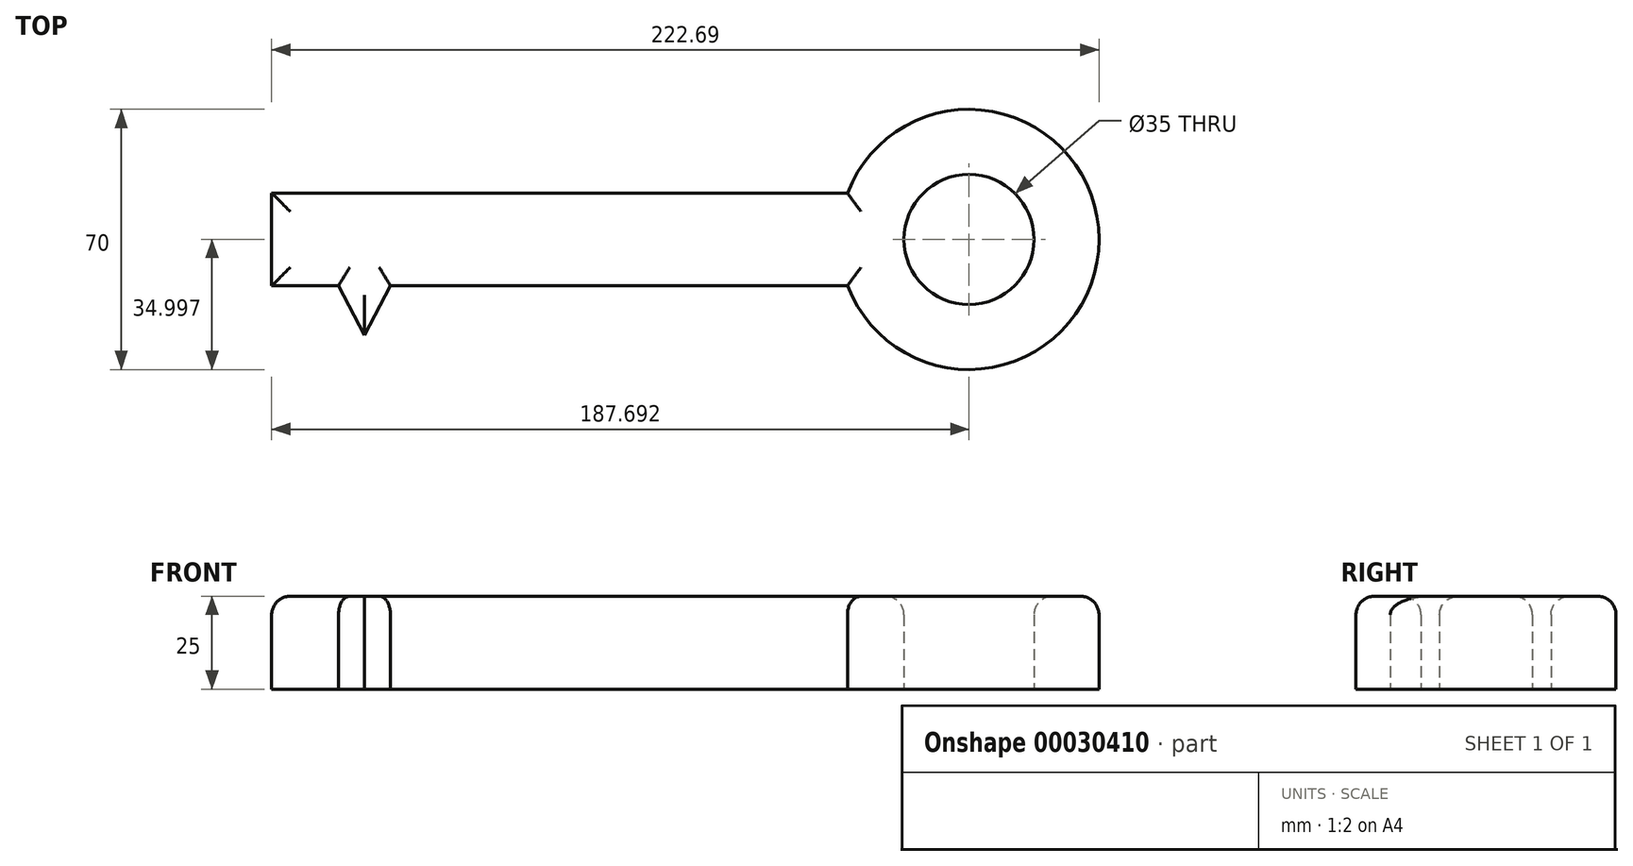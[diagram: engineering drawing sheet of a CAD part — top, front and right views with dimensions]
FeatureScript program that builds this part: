
annotation { "Feature Type Name" : "Feature", "Feature Type Description" : "" }
export const myFeature = defineFeature(function(context is Context, id is Id, definition is map)
    precondition{}
    {
        {
            var Q0;
            Q0=qCreatedBy(makeId("Top.planeOp"),FACE);
            var sketch = newSketch(context, id + "F0", { "sketchPlane" : qUnion([Q0])});
            skLineSegment(sketch, "E0.bottom", {"start": v(-155, 3.98) * mm, "end": v(0, 3.98) * mm});
            skLineSegment(sketch, "E0.top", {"start": v(-155, -21.02) * mm, "end": v(0, -21.02) * mm});
            skLineSegment(sketch, "E0.left", {"start": v(-155, 3.98) * mm, "end": v(-155, -21.02) * mm});
            skLineSegment(sketch, "E1.bottom", {"start": v(-155, -21.02) * mm, "end": v(-145, -21.02) * mm});
            skLineSegment(sketch, "E1.top", {"start": v(-155, -51.02) * mm, "end": v(-145, -51.02) * mm});
            skLineSegment(sketch, "E1.left", {"start": v(-155, -21.02) * mm, "end": v(-155, -51.02) * mm});
            skLineSegment(sketch, "E1.right", {"start": v(-145, -21.02) * mm, "end": v(-145, -51.02) * mm});
            skLineSegment(sketch, "E2.bottom", {"start": v(-155, -21.02) * mm, "end": v(-147, -21.02) * mm});
            skLineSegment(sketch, "E2.top", {"start": v(-155, -36.02) * mm, "end": v(-147, -36.02) * mm});
            skLineSegment(sketch, "E2.left", {"start": v(-155, -21.02) * mm, "end": v(-155, -36.02) * mm});
            skLineSegment(sketch, "E2.right", {"start": v(-147, -21.02) * mm, "end": v(-147, -36.02) * mm});
            skLineSegment(sketch, "E3", {"start": v(-137, -21.02) * mm, "end": v(-130, -34.29) * mm});
            skLineSegment(sketch, "E4", {"start": v(-130, -34.29) * mm, "end": v(-123, -21.02) * mm});
            skArc(sketch, "E5", {"start": v(0, -21.02) * mm, "mid": v(67.7, -8.52) * mm, "end": v(0, 3.98) * mm});
            skCircle(sketch, "E6", {"center": v(32.7, -8.52) * mm, "radius": 17.5 * mm});
            skLineSegment(sketch, "E7", {"start": v(-155, -8.52) * mm, "end": v(32.7, -8.52) * mm, "construction": true});
            skSolve(sketch);
        }
        {
            var Q0;
            Q0=makeQuery(id+"F0.imprint","IMPRINT",FACE,{"disambiguationData":[TD([[makeQuery(id+"F0.imprint","IMPRINT",EDGE,{"derivedFrom":sQuery(id+"F0.wireOp",EDGE,"E0.bottom")}),-1.0]])]});
            var Q1;
            Q1=makeQuery(id+"F0.imprint","IMPRINT",FACE,{"disambiguationData":[TD([[makeQuery(id+"F0.imprint","IMPRINT",EDGE,{"derivedFrom":sQuery(id+"F0.wireOp",EDGE,"E2.bottom")}),-1.0]])]});
            var Q2;
            Q2=makeQuery(id+"F0.imprint","IMPRINT",FACE,{"disambiguationData":[TD([[makeQuery(id+"F0.imprint","IMPRINT",EDGE,{"derivedFrom":sQuery(id+"F0.wireOp",EDGE,"E1.bottom")}),-1.0]])]});
            var Q3;
            {var subQ1=sQuery(id+"F0.wireOp",EDGE,"E3");Q3=makeQuery(id+"F0.imprint","IMPRINT",FACE,{"disambiguationData":[TD([[makeQuery(id+"F0.imprint","IMPRINT",EDGE,{"derivedFrom":subQ1}),1.0]])]});}
            extrude(context, id + "F1", {"entities" : qUnion([Q0, Q1, Q2, Q3]), "depth" : 25 * mm});
        }
        {
            var Q0;
            Q0=makeQuery(id+"F1.opExtrude","CAP_EDGE",EDGE,{"disambiguationData":[OSD([sQuery(id+"F0.wireOp",EDGE,"E0.bottom")])],"isStart":false});
            var Q1;
            {var subQ0=sQuery(id+"F0.wireOp",EDGE,"E0.top");Q1=makeQuery(id+"F1.opExtrude","CAP_EDGE",EDGE,{"disambiguationData":[OSD([subQ0]),TDD([makeQuery(id+"F0.imprint","IMPRINT",EDGE,{"disambiguationData":[TD([[makeQuery(id+"F0.imprint","INTERSECT",VERTEX,{"derivedFrom":[subQ0,sQuery(id+"F0.wireOp",EDGE,"E5")]}),1.0]])],"derivedFrom":subQ0})])],"isStart":false});}
            var Q2;
            Q2=makeQuery(id+"F1.opExtrude","CAP_EDGE",EDGE,{"disambiguationData":[OSD([sQuery(id+"F0.wireOp",EDGE,"E3")])],"isStart":false});
            var Q3;
            Q3=makeQuery(id+"F1.opExtrude","CAP_EDGE",EDGE,{"disambiguationData":[OSD([sQuery(id+"F0.wireOp",EDGE,"E0.left"),sQuery(id+"F0.wireOp",EDGE,"E1.left"),sQuery(id+"F0.wireOp",EDGE,"E2.left")])],"isStart":false});
            var Q4;
            Q4=makeQuery(id+"F1.opExtrude","CAP_EDGE",EDGE,{"disambiguationData":[OSD([sQuery(id+"F0.wireOp",EDGE,"E1.right")])],"isStart":false});
            var Q5;
            Q5=makeQuery(id+"F1.opExtrude","CAP_FACE",FACE,{"disambiguationData":[OSD([sQuery(id+"F0.wireOp",EDGE,"E0.bottom"),sQuery(id+"F0.wireOp",EDGE,"E0.top"),sQuery(id+"F0.wireOp",EDGE,"E0.left"),sQuery(id+"F0.wireOp",EDGE,"E1.top"),sQuery(id+"F0.wireOp",EDGE,"E1.left"),sQuery(id+"F0.wireOp",EDGE,"E1.right"),sQuery(id+"F0.wireOp",EDGE,"E2.left"),sQuery(id+"F0.wireOp",EDGE,"E3"),sQuery(id+"F0.wireOp",EDGE,"E4"),sQuery(id+"F0.wireOp",EDGE,"E5"),sQuery(id+"F0.wireOp",EDGE,"E6")])],"isStart":false});
            var Q6;
            Q6=makeQuery(id+"F1.opExtrude","CAP_EDGE",EDGE,{"disambiguationData":[OSD([sQuery(id+"F0.wireOp",EDGE,"E6")])],"isStart":false});
            fillet(context, id + "F2", {"entities" : qUnion([Q0, Q1, Q2, Q3, Q4, Q5, Q6]), "radius" : 5 * mm, "tangentPropagation" : true, "allowEdgeOverflow" : false});
        }
    });
